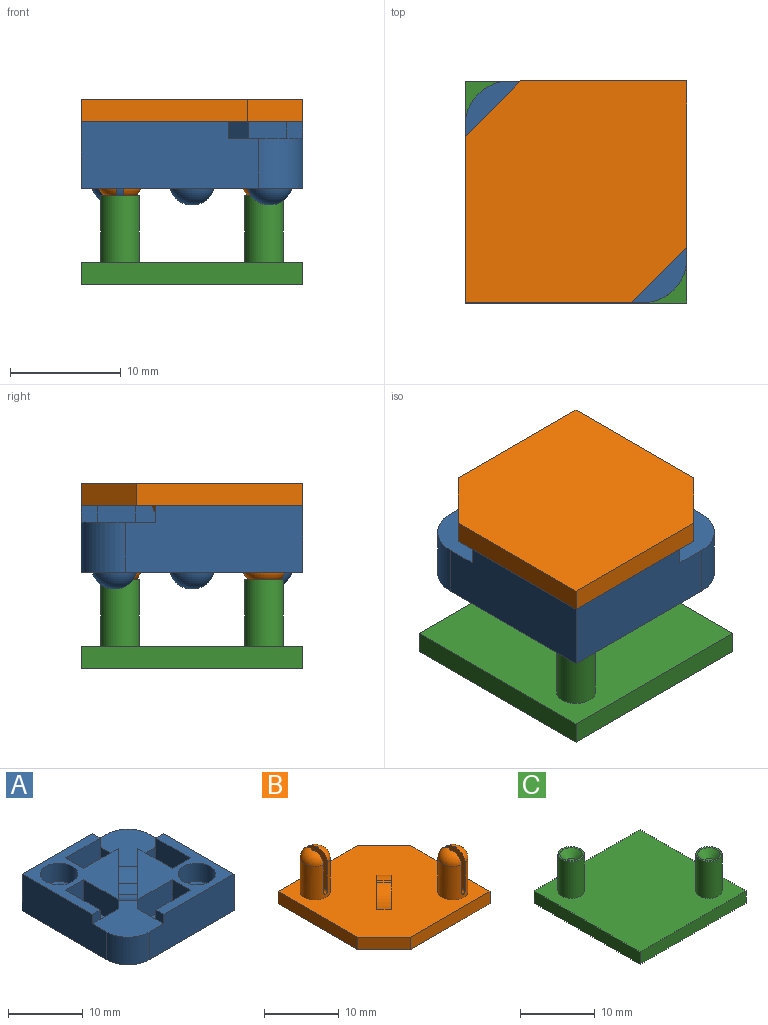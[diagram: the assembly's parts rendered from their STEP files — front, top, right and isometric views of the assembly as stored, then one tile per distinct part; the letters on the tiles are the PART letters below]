
ASSEMBLY  parts=3 mates=4
PART A: 54 faces, bbox 20x20x7.5 mm
  f0: plane 8.16x8.16mm, normal (0,0,1), area 45.7mm2, adj f8,f10,f12,f13,f31,f34,f35,f36
  f1: plane 8.16x8.16mm, normal (0,0,1), area 45.7mm2, adj f6,f7,f9,f11,f31,f32,f33,f34
  f2: cylinder r=2.05mm len=4.1mm, axis (0,0,1), area 27.9mm2, adj f14,f52
  f3: cylinder r=2.05mm len=4.1mm, axis (0,0,1), area 27.9mm2, adj f14,f53
  f4: plane 13.25x13.25mm, normal (0,0,1), area 76.9mm2, adj f6,f8,f15,f16,f17,f27,f28,f29
  f5: plane 13.25x13.25mm, normal (0,0,1), area 76.9mm2, adj f7,f13,f19,f20,f21,f23,f24,f25
  f6: plane 16x6mm, normal (-1,0,0), area 91.9mm2, adj f1,f4,f8,f14,f32,f37
  f7: plane 16x6mm, normal (0,-1,0), area 91.9mm2, adj f1,f5,f13,f14,f33,f37
  f8: plane 16x6mm, normal (0,1,0), area 91.9mm2, adj f0,f4,f6,f14,f36,f38
  f9: plane 3.4x2.5mm, normal (0,1,0), area 8.5mm2, adj f1,f15,f17,f18
  f10: plane 3.4x2.5mm, normal (0,-1,0), area 8.5mm2, adj f0,f19,f21,f22
  f11: plane 3.4x2.5mm, normal (1,0,0), area 8.5mm2, adj f1,f23,f25,f26
  f12: plane 3.4x2.5mm, normal (-1,0,0), area 8.5mm2, adj f0,f27,f29,f30
  f13: plane 16x6mm, normal (1,0,0), area 91.9mm2, adj f0,f5,f7,f14,f35,f38
  f14: plane 20x20mm, normal (0,0,-1), area 316.5mm2, adj f2,f3,f6,f7,f8,f13,f37,f38
  f15: plane 6.5x4mm, normal (-1,0,0), area 26mm2, adj f4,f9,f16,f18,f31
  f16: plane 4x3.4mm, normal (0,-1,0), area 13.6mm2, adj f4,f15,f17,f18
  f17: plane 6.5x4mm, normal (1,0,0), area 26mm2, adj f4,f9,f16,f18,f32
  f18: plane 6.5x3.4mm, normal (0,0,1), area 22.1mm2, adj f9,f15,f16,f17
  f19: plane 6.5x4mm, normal (1,0,0), area 26mm2, adj f5,f10,f20,f22,f34
  f20: plane 4x3.4mm, normal (0,1,0), area 13.6mm2, adj f5,f19,f21,f22
  f21: plane 6.5x4mm, normal (-1,0,0), area 26mm2, adj f5,f10,f20,f22,f35
  f22: plane 6.5x3.4mm, normal (0,0,1), area 22.1mm2, adj f10,f19,f20,f21
  f23: plane 6.5x4mm, normal (0,1,0), area 26mm2, adj f5,f11,f24,f26,f33
  f24: plane 4x3.4mm, normal (-1,0,0), area 13.6mm2, adj f5,f23,f25,f26
  f25: plane 6.5x4mm, normal (0,-1,0), area 26mm2, adj f5,f11,f24,f26,f34
  f26: plane 6.5x3.4mm, normal (0,0,1), area 22.1mm2, adj f11,f23,f24,f25
  f27: plane 6.5x4mm, normal (0,-1,0), area 26mm2, adj f4,f12,f28,f30,f36
  f28: plane 4x3.4mm, normal (1,0,0), area 13.6mm2, adj f4,f27,f29,f30
  f29: plane 6.5x4mm, normal (0,1,0), area 26mm2, adj f4,f12,f28,f30,f31
  f30: plane 6.5x3.4mm, normal (0,0,1), area 22.1mm2, adj f12,f27,f28,f29
  f31: plane 8.35x8.35mm, normal (0.71,-0.71,0), area 23.9mm2, adj f0,f1,f4,f15,f29,f41,f50,f51
  f32: plane 1.5x1.5mm, normal (0,-1,0), area 2.3mm2, adj f1,f4,f6,f17
  f33: plane 1.5x1.5mm, normal (-1,0,0), area 2.3mm2, adj f1,f5,f7,f23
  f34: plane 8.35x8.35mm, normal (-0.71,0.71,0), area 23.9mm2, adj f0,f1,f5,f19,f25,f41,f50,f51
  f35: plane 1.5x1.5mm, normal (0,1,0), area 2.3mm2, adj f0,f5,f13,f21
  f36: plane 1.5x1.5mm, normal (1,0,0), area 2.3mm2, adj f0,f4,f8,f27
  f37: cylinder r=4mm len=4.5mm, axis (0,0,1), area 28.3mm2, adj f1,f6,f7,f14
  f38: cylinder r=4mm len=4.5mm, axis (0,0,1), area 28.3mm2, adj f0,f8,f13,f14
  f39: cylinder r=2.5mm len=5mm, axis (0,0,1), area 47.1mm2, adj f5,f53
  f40: cylinder r=2.5mm len=5mm, axis (0,0,1), area 47.1mm2, adj f4,f52
  f41: plane 3.63x3.63mm, normal (0,0,1), area 6.6mm2, adj f31,f34,f50,f51
  f42: plane 0.13x0.13mm, normal (0,0,-1), area 0mm2, adj f49
  f43: plane 0.13x0.13mm, normal (0,0,-1), area 0mm2, adj f48
  f44: plane 0.13x0.13mm, normal (0,0,-1), area 0mm2, adj f47
  f45: plane 0.13x0.13mm, normal (0,0,-1), area 0mm2, adj f46
  f46: torus R=0.06mm, axis (0,0,1), area 19.9mm2, adj f14,f45
  f47: torus R=0.06mm, axis (0,0,1), area 19.9mm2, adj f14,f44
  f48: torus R=0.06mm, axis (0,0,1), area 19.9mm2, adj f14,f43
  f49: torus R=0.06mm, axis (0,0,1), area 19.9mm2, adj f14,f42
  f50: cylinder r=4mm len=3.72mm, axis (0.71,-0.71,0), area 7.6mm2, adj f1,f31,f34,f41
  f51: cylinder r=4mm len=3.72mm, axis (-0.71,0.71,0), area 7.6mm2, adj f0,f31,f34,f41
  f52: torus R=3.05mm, axis (0,0,1), area 13.7mm2, adj f2,f40
  f53: torus R=3.05mm, axis (0,0,1), area 13.7mm2, adj f3,f39
PART B: 31 faces, bbox 20x20x9 mm
  f0: cylinder r=2mm len=5.5mm, axis (0,0,-1), area 62.4mm2, adj f4,f9,f17,f21,f22,f23,f24
  f1: plane 0.71x0.15mm, normal (0,0,1), area 0.1mm2, adj f17,f21
  f2: cylinder r=2mm len=5.5mm, axis (0,0,-1), area 62.4mm2, adj f5,f9,f18,f19,f20,f25,f26
  f3: plane 0.71x0.15mm, normal (0,0,1), area 0.1mm2, adj f18,f19
  f4: torus R=0.5mm, axis (0,0,1), area 9.1mm2, adj f0,f15,f22
  f5: torus R=0.5mm, axis (0,0,1), area 9.1mm2, adj f2,f16,f20
  f6: plane 5.15x5.15mm, normal (-0.71,0.71,0), area 10.5mm2, adj f8,f9,f27,f28
  f7: plane 5.15x5.15mm, normal (0.71,-0.71,0), area 10.5mm2, adj f8,f9,f27,f28
  f8: plane 1.67x1.67mm, normal (0,0,1), area 0.7mm2, adj f6,f7,f27,f28
  f9: plane 20x20mm, normal (0,0,1), area 335.3mm2, adj f0,f2,f6,f7,f10,f11,f12,f13
  f10: plane 15x2mm, normal (0,-1,0), area 30mm2, adj f9,f11,f14,f30
  f11: plane 15x2mm, normal (1,0,0), area 30mm2, adj f9,f10,f14,f29
  f12: plane 15x2mm, normal (0,1,0), area 30mm2, adj f9,f13,f14,f29
  f13: plane 15x2mm, normal (-1,0,0), area 30mm2, adj f9,f12,f14,f30
  f14: plane 20x20mm, normal (0,0,-1), area 375mm2, adj f10,f11,f12,f13,f29,f30
  f15: plane 0.71x0.15mm, normal (0,0,1), area 0.1mm2, adj f4,f22
  f16: plane 0.71x0.15mm, normal (0,0,1), area 0.1mm2, adj f5,f20
  f17: torus R=0.5mm, axis (0,0,1), area 9.1mm2, adj f0,f1,f21
  f18: torus R=0.5mm, axis (0,0,1), area 9.1mm2, adj f2,f3,f19
  f19: plane 6x3.94mm, normal (1,0,0), area 22.6mm2, adj f2,f3,f18,f25
  f20: plane 6x3.94mm, normal (-1,0,0), area 22.6mm2, adj f2,f5,f16,f26
  f21: plane 6x3.94mm, normal (1,0,0), area 22.6mm2, adj f0,f1,f17,f23
  f22: plane 6x3.94mm, normal (-1,0,0), area 22.6mm2, adj f0,f4,f15,f24
  f23: cylinder r=0.5mm len=4mm, axis (0,-1,0), area 2.5mm2, adj f0,f21,f24
  f24: cylinder r=0.5mm len=4mm, axis (0,1,0), area 2.5mm2, adj f0,f22,f23
  f25: cylinder r=0.5mm len=4mm, axis (0,-1,0), area 2.5mm2, adj f2,f19,f26
  f26: cylinder r=0.5mm len=4mm, axis (0,1,0), area 2.5mm2, adj f2,f20,f25
  f27: cylinder r=4mm len=3.86mm, axis (-0.71,0.71,0), area 8.4mm2, adj f6,f7,f8,f9
  f28: cylinder r=4mm len=3.86mm, axis (-0.71,0.71,0), area 8.4mm2, adj f6,f7,f8,f9
  f29: plane 5x5mm, normal (0.71,0.71,0), area 14.1mm2, adj f9,f11,f12,f14
  f30: plane 5x5mm, normal (-0.71,-0.71,0), area 14.1mm2, adj f9,f10,f13,f14
PART C: 14 faces, bbox 20x20x8 mm
  f0: plane 20x2mm, normal (-1,0,0), area 40mm2, adj f1,f3,f4,f5
  f1: plane 20x2mm, normal (0,-1,0), area 40mm2, adj f0,f2,f4,f5
  f2: plane 20x2mm, normal (1,0,0), area 40mm2, adj f1,f3,f4,f5
  f3: plane 20x2mm, normal (0,1,0), area 40mm2, adj f0,f2,f4,f5
  f4: plane 20x20mm, normal (0,0,1), area 380.8mm2, adj f0,f1,f2,f3,f6,f8
  f5: plane 20x20mm, normal (0,0,-1), area 400mm2, adj f0,f1,f2,f3
  f6: cylinder r=1.75mm len=6mm, axis (0,0,-1), area 66mm2, adj f4,f7
  f7: plane 3.5x3.5mm, normal (0,0,1), area 2.6mm2, adj f6,f13
  f8: cylinder r=1.75mm len=6mm, axis (0,0,-1), area 66mm2, adj f4,f9
  f9: plane 3.5x3.5mm, normal (0,0,1), area 2.6mm2, adj f8,f12
  f10: plane 1x1mm, normal (0,0,1), area 0.8mm2, adj f12
  f11: plane 1x1mm, normal (0,0,1), area 0.8mm2, adj f13
  f12: cone r=0.5mm half-angle=45deg, axis (0,0,1), area 8.9mm2, adj f9,f10
  f13: cone r=0.5mm half-angle=45deg, axis (0,0,1), area 8.9mm2, adj f7,f11
PLACE A rot(axis=(0,0,-1),90deg) t=(3.72,17.12,18.98)mm
PLACE B rot(axis=(1,0,0),180deg) t=(42.27,17.12,26.98)mm
PLACE C rot(axis=(0,0,1),90deg) t=(23.72,-31.32,10.31)mm
MATE cylindrical B.f2 <-> A.f2  axis (0,0,1) through (20.22,13.62,22.23)mm
MATE slider C.f8 <-> A.f2  axis (0,0,-1) through (20.22,13.62,15.31)mm
MATE slider C.f6 <-> A.f3  axis (0,0,-1) through (7.22,0.62,15.31)mm
MATE cylindrical B.f0 <-> A.f3  axis (0,0,1) through (7.22,0.62,19.48)mm
